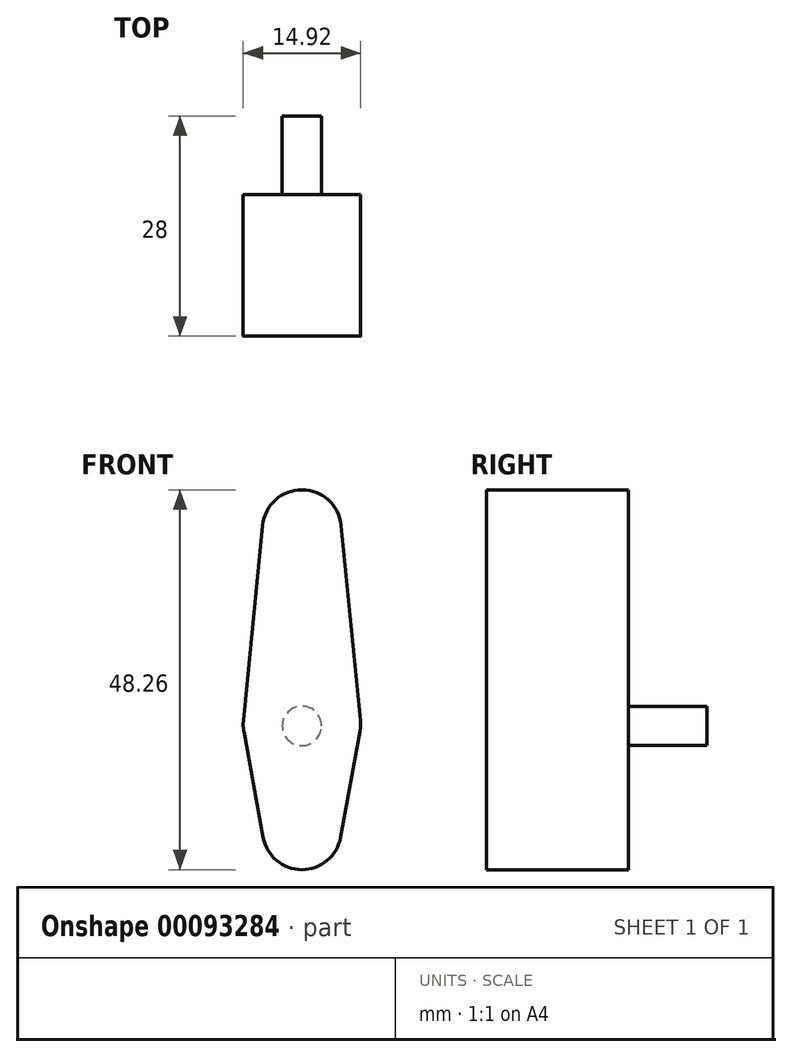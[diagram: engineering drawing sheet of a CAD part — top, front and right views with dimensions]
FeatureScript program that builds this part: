
annotation { "Feature Type Name" : "Feature", "Feature Type Description" : "" }
export const myFeature = defineFeature(function(context is Context, id is Id, definition is map)
    precondition{}
    {
        {
            var Q0;
            Q0=qCreatedBy(makeId("Front.planeOp"),FACE);
            var sketch = newSketch(context, id + "F0", { "sketchPlane" : qUnion([Q0])});
            skLineSegment(sketch, "E0.bottom", {"start": v(0, 30) * mm, "end": v(0, 30) * mm});
            skLineSegment(sketch, "E0.top", {"start": v(0, -18.26) * mm, "end": v(0, -18.26) * mm});
            skLineSegment(sketch, "E0.left", {"start": v(0, 30) * mm, "end": v(0, -18.26) * mm});
            skLineSegment(sketch, "E0.right", {"start": v(-4.98, 25.5) * mm, "end": v(-7.43, 0.7) * mm});
            skLineSegment(sketch, "E1", {"start": v(-7.37, -0.7) * mm, "end": v(-4.92, -14.16) * mm});
            skLineSegment(sketch, "E2", {"start": v(-7.5, 0) * mm, "end": v(0, 0) * mm, "construction": true});
            skPoint(sketch, "E3.visualSharp", {"position": v(-4.53, 30) * mm});
            skArc(sketch, "E3.filletArc", {"start": v(0, 30) * mm, "mid": v(-3.36, 28.7) * mm, "end": v(-4.98, 25.5) * mm});
            skPoint(sketch, "E4.visualSharp", {"position": v(-4.17, -18.26) * mm});
            skArc(sketch, "E4.filletArc", {"start": v(-4.92, -14.16) * mm, "mid": v(-3.2, -17.1) * mm, "end": v(0, -18.26) * mm});
            skPoint(sketch, "E5.visualSharp", {"position": v(-7.5, 0) * mm});
            skArc(sketch, "E5.filletArc", {"start": v(-7.43, 0.7) * mm, "mid": v(-7.45, 0) * mm, "end": v(-7.37, -0.7) * mm});
            skSolve(sketch);
        }
        {
            var Q0;
            Q0=makeQuery(id+"F0.imprint","IMPRINT",FACE,{"disambiguationData":[TD([[makeQuery(id+"F0.imprint","IMPRINT",EDGE,{"derivedFrom":sQuery(id+"F0.wireOp",EDGE,"E0.left")}),-1.0]])]});
            var Q1;
            Q1 = qSketchRegion(id + "F0", true);
            extrude(context, id + "F1", {"entities" : qUnion([Q0, Q1]), "depth" : 18 * mm});
        }
        {
            var Q0;
            Q0=makeQuery(id+"F1.opExtrude","SWEPT_BODY",BODY,{"disambiguationData":[OSD([sQuery(id+"F0.wireOp",EDGE,"E0.left"),sQuery(id+"F0.wireOp",EDGE,"E0.right"),sQuery(id+"F0.wireOp",EDGE,"E1"),sQuery(id+"F0.wireOp",EDGE,"E3.filletArc"),sQuery(id+"F0.wireOp",EDGE,"E4.filletArc"),sQuery(id+"F0.wireOp",EDGE,"E5.filletArc")])]});
            var Q1;
            Q1=qCreatedBy(makeId("Right.planeOp"),FACE);
            mirror(context, id + "F2", {"operationType" : NewBodyOperationType.ADD, "entities" : qUnion([Q0]), "mirrorPlane" : qUnion([Q1])});
        }
        {
            var Q0;
            {var subQ0=makeQuery(id+"F1.opExtrude","CAP_FACE",FACE,{"disambiguationData":[OSD([sQuery(id+"F0.wireOp",EDGE,"E0.left"),sQuery(id+"F0.wireOp",EDGE,"E0.right"),sQuery(id+"F0.wireOp",EDGE,"E1"),sQuery(id+"F0.wireOp",EDGE,"E3.filletArc"),sQuery(id+"F0.wireOp",EDGE,"E4.filletArc"),sQuery(id+"F0.wireOp",EDGE,"E5.filletArc")])],"isStart":true});Q0=makeQuery(id+"F2.boolean.opBoolean","MERGE",FACE,{"derivedFrom":[subQ0,makeQuery(id+"F2.opPattern","COPY",FACE,{"derivedFrom":subQ0,"instanceName":"1"})]});}
            var sketch = newSketch(context, id + "F3", { "sketchPlane" : qUnion([Q0])});
            skCircle(sketch, "E6", {"center": v(0, 0) * mm, "radius": 2.5 * mm});
            skSolve(sketch);
        }
        {
            var Q0;
            Q0 = qSketchRegion(id + "F3", true);
            extrude(context, id + "F4", {"entities" : qUnion([Q0]), "operationType" : NewBodyOperationType.ADD, "depth" : 10 * mm});
        }
    });
